# Revit family: Lighting_Linear_LED_StarTek_Micro-Flat-Direct1
name_source: partatom
category: Lighting Fixtures
units: mm (PartAtom-declared; Revit-internal decimal feet)

## family parameters
Cut with Voids When Loaded = No
Host = Face
Light Source = Yes
OmniClass Number = 23.80.70.11
OmniClass Title = Luminaries for Internal Lighting
Part Type = Normal
Room Calculation Point = No
Round Connector Dimension = Use Diameter
Shared = No

## types (1)
- Default - please load Revit Family Type Catalog
    ****Power Options = This fixture has remote power options only.  RSMXXX - Remote Surface Mount or RIWXXX - Remote in Wall. Available in White (W) or Black (B). Available in 10', 25', 50', 75' , & 100'.
    Apparent Load = 13 VA
    Assembly Code = D5020200
    CRI = 80
    Color Filter = 16777215
    Default Elevation = 48 "
    Description = Micro Flat Direct
    Dimming Lamp Color Temperature Shift = <None>
    Distribution = SD-SatinIce Diffused
    Emit Shape Visible in Rendering = No
    Emit from Rectangle Length = 47.88 "
    Emit from Rectangle Width = 0.82 "
    Frequency = 60 Hz
    Height = 2 "
    Input Wattage = 12 W
    Keynote = 16500
    Lamp = LED
    Length = 48 "
    Manufacturer = StarTek Lighting
    Model = MFLAT
    Number of Poles = 1
    Phase = 1
    Photometric Note = Import IES files https://starteklightingamerica.com
    Photometric Web File = Generic Light Source Shown : Please download and link the IES file that best matches your fixture specification
    Power Factor = 0.93
    Product data url = https://bimobject.com
    Tilt Angle = 90.00°
    URL = https://starteklightingamerica.com
    Voltage = 120 V
    Voltage Range = 120-277V
    Wattage Comments = Efficacy up to 120 lm/W
    Weight = 0.00 lbf
    Width = 1.44 "
    Z_TB1 = T-Grid Mount : TB1 - 9/16" Grid
    Z_TB2 = T-Grid Mount : TB2 - 15/16" Grid
    Z_TB3 = T-Grid Mount : TB3 - 9/16" Grid (Tegular)
    Z_TB4 = T-Grid Mount : TB4 - 15/16" Grid (Tegular)
    Z_TB5 = T-Grid Mount : TB5 - 9/16" Bolt Slotted T-Grid

## geometry (parser evidence)
native form markers: Sweep x9
no freeform markers — native parametric forms only
